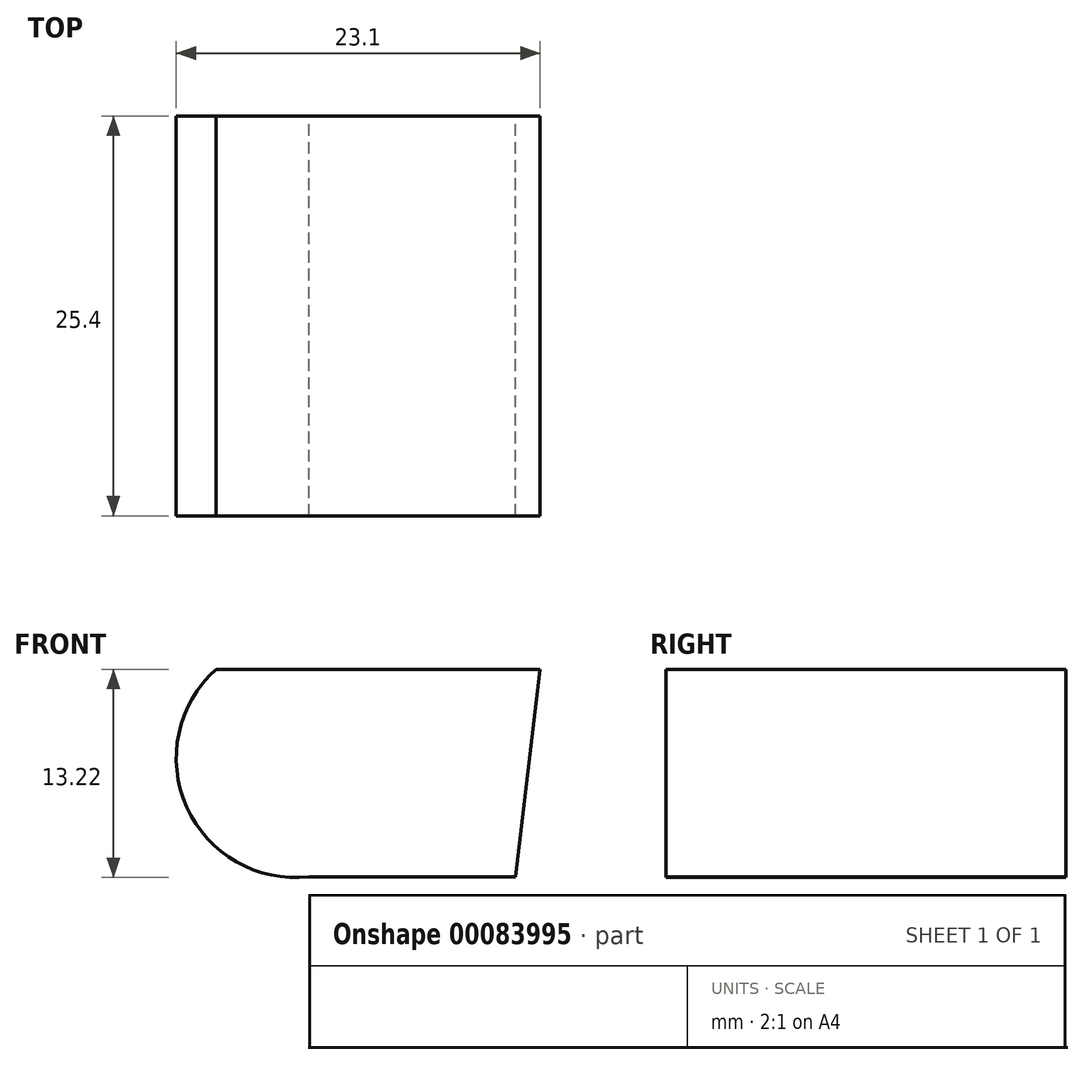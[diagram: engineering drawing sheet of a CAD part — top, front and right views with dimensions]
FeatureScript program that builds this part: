
annotation { "Feature Type Name" : "Feature", "Feature Type Description" : "" }
export const myFeature = defineFeature(function(context is Context, id is Id, definition is map)
    precondition{}
    {
        {
            var Q0;
            Q0=qCreatedBy(makeId("Front.planeOp"),FACE);
            var sketch = newSketch(context, id + "F0", { "sketchPlane" : qUnion([Q0])});
            skArc(sketch, "E0", {"start": v(-26.81, 18.87) * mm, "mid": v(-39.29, 26.14) * mm, "end": v(-33.38, 12.96) * mm});
            skLineSegment(sketch, "E1", {"start": v(-18.7, 26.14) * mm, "end": v(-39.29, 26.14) * mm});
            skPoint(sketch, "E1.startSnap0", {"position": v(-39.29, 26.14) * mm});
            skLineSegment(sketch, "E2", {"start": v(-33.38, 12.96) * mm, "end": v(-20.24, 12.96) * mm});
            skLineSegment(sketch, "E3", {"start": v(-20.24, 12.96) * mm, "end": v(-18.7, 26.14) * mm});
            skLineSegment(sketch, "E4", {"start": v(-20.24, 12.96) * mm, "end": v(-15.76, 12.44) * mm});
            skLineSegment(sketch, "E5", {"start": v(-15.76, 12.44) * mm, "end": v(-15.76, 23.57) * mm});
            skLineSegment(sketch, "E6", {"start": v(-18.7, 26.14) * mm, "end": v(-15.76, 23.57) * mm});
            skLineSegment(sketch, "E7", {"start": v(-39.29, 26.14) * mm, "end": v(-39.29, 32.04) * mm});
            skLineSegment(sketch, "E8", {"start": v(-39.29, 32.04) * mm, "end": v(-18.7, 32.04) * mm});
            skLineSegment(sketch, "E9", {"start": v(-18.7, 32.04) * mm, "end": v(-18.7, 26.14) * mm});
            skLineSegment(sketch, "E10", {"start": v(-31.5, 17.76) * mm, "end": v(36.25, 30.94) * mm});
            skLineSegment(sketch, "E11", {"start": v(36.25, 30.94) * mm, "end": v(-29, 26.14) * mm});
            skSolve(sketch);
        }
        {
            var Q0;
            {var subQ7=sQuery(id+"F0.wireOp",EDGE,"E2");Q0=makeQuery(id+"F0.imprint","IMPRINT",FACE,{"disambiguationData":[TD([[makeQuery(id+"F0.imprint","IMPRINT",EDGE,{"derivedFrom":subQ7}),1.0]])]});}
            extrude(context, id + "F1", {"entities" : qUnion([Q0]), "depth" : 25.4 * mm});
        }
    });
